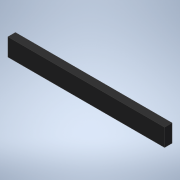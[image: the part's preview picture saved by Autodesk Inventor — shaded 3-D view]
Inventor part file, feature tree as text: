
AUTODESK INVENTOR PART (.ipt)
format: ipt  version: 2020 (Build 240168000, 168)  size: 97,792 bytes
history: native  units: mm
features: other x1, extrude x1
ambient origin geometry x8: Origin, YZ Plane, XZ Plane, XY Plane, X Axis, Y Axis, Z Axis, Center Point
bodies: Body1 (feature_tree)
feature tree (2):
  other  "實體1"
  extrude  "擠出1"  Depth=14.0mm
